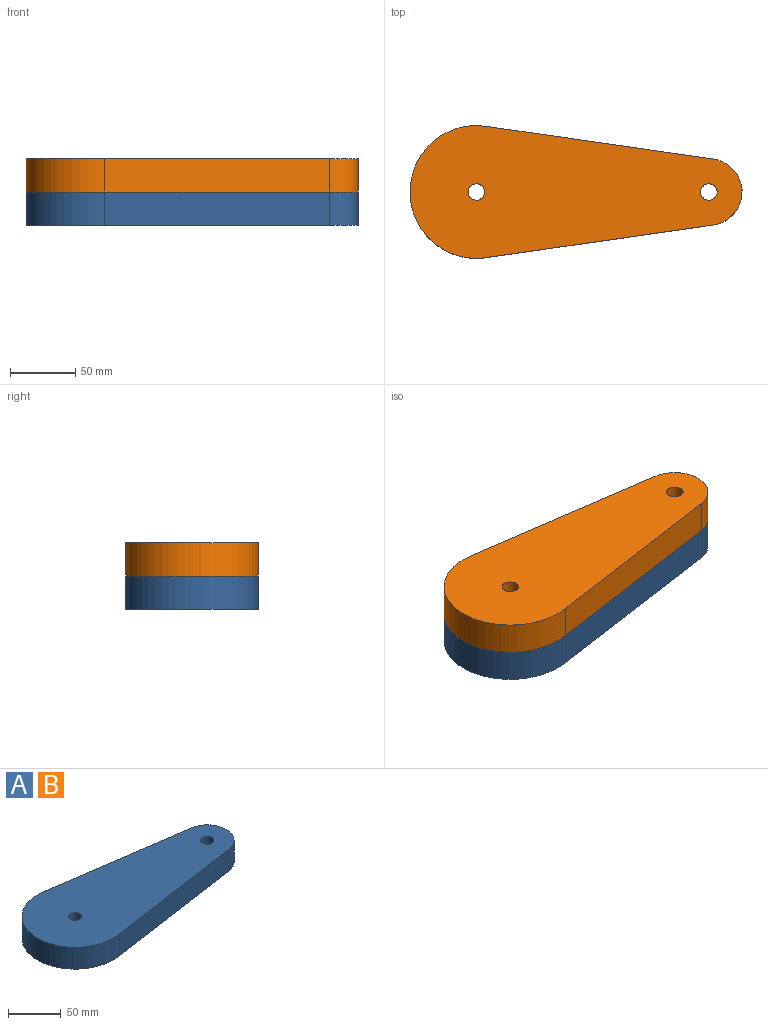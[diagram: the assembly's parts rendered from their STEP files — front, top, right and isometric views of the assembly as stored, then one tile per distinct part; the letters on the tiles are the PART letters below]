
ASSEMBLY  parts=2 mates=1
PART A: 8 faces, bbox 254x101.6x25.4 mm
  f0: cylinder r=50.8mm len=101.6mm, axis (0,0,-1), area 4478.6mm2, adj f1,f3,f4,f5
  f1: plane 172.03x25.4mm, normal (0.14,-0.99,0), area 4414.6mm2, adj f0,f2,f4,f5
  f2: cylinder r=25.4mm len=50.28mm, axis (0,0,-1), area 1842mm2, adj f1,f3,f4,f5
  f3: plane 174.17x25.4mm, normal (0.14,0.99,0), area 4469.8mm2, adj f0,f2,f4,f5
  f4: plane 254x101.6mm, normal (0,0,1), area 18496.5mm2, adj f0,f1,f2,f3,f6,f7
  f5: plane 254x101.6mm, normal (0,0,-1), area 18496.5mm2, adj f0,f1,f2,f3,f6,f7
  f6: cylinder r=6.35mm len=25.4mm, axis (0,0,1), area 1013.4mm2, adj f4,f5
  f7: cylinder r=6.35mm len=25.4mm, axis (0,0,1), area 1013.4mm2, adj f4,f5
PART B: same geometry as A
PLACE A t=(-15.43,32.76,37.71)mm
PLACE B t=(-15.43,32.76,63.11)mm
MATE planar A.f4 <-> B.f5  axis (0,0,1) through (-44.13,32.77,63.11)mm
